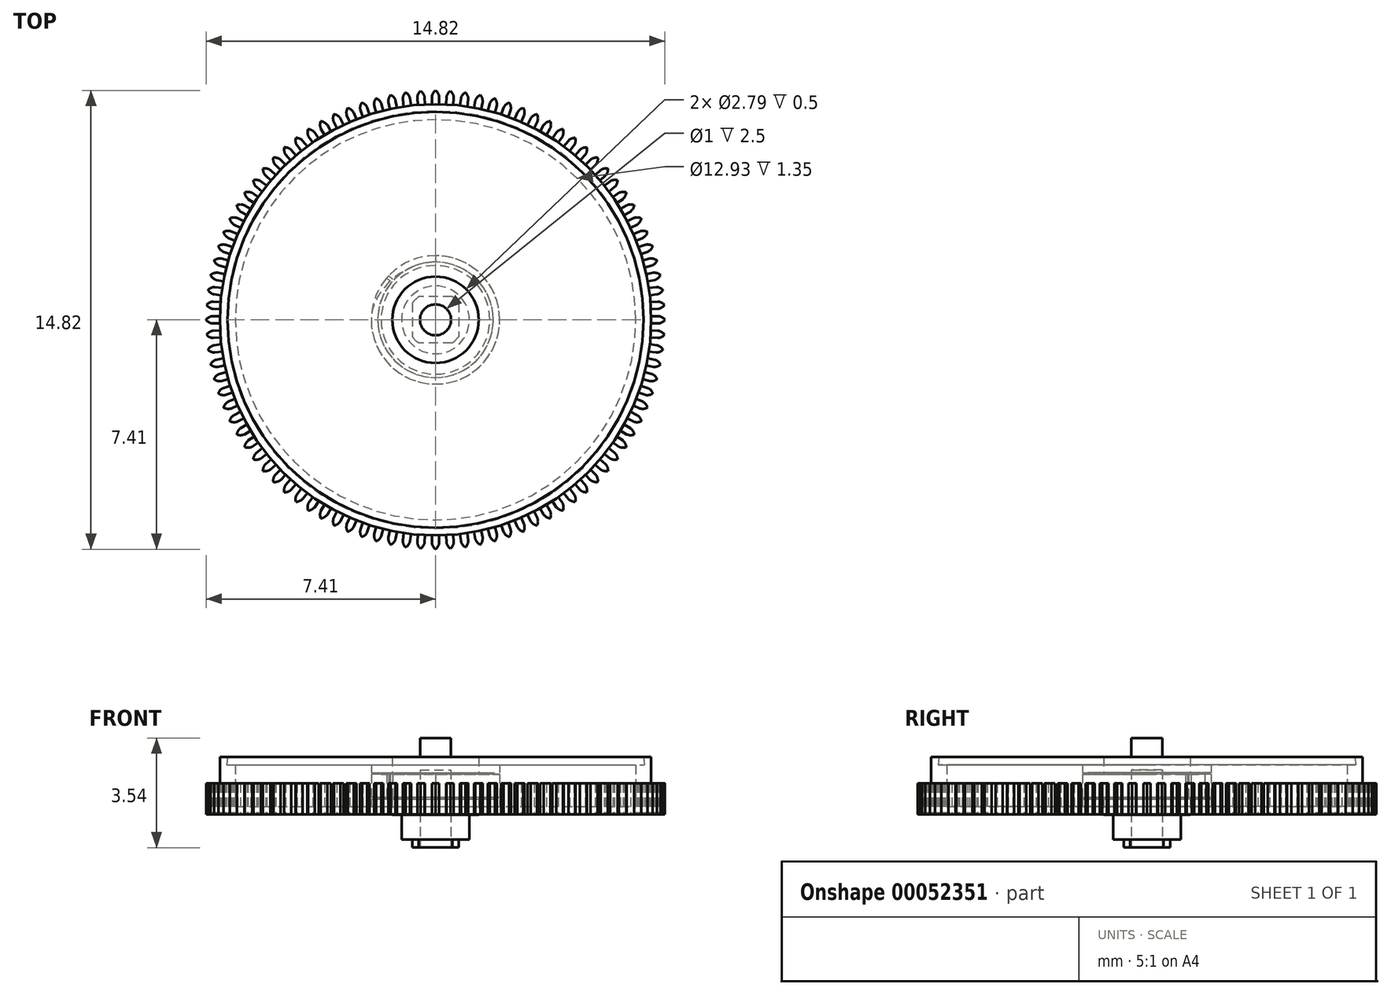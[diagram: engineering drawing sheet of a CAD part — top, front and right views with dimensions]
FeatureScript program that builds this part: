
annotation { "Feature Type Name" : "Feature", "Feature Type Description" : "" }
export const myFeature = defineFeature(function(context is Context, id is Id, definition is map)
    precondition{}
    {
        {
            var Q0;
            Q0=qCreatedBy(makeId("Front.planeOp"),FACE);
            var sketch = newSketch(context, id + "F0", { "sketchPlane" : qUnion([Q0])});
            skLineSegment(sketch, "E0", {"start": v(0, 0) * mm, "end": v(-2.08, 0) * mm, "construction": true});
            skLineSegment(sketch, "E1", {"start": v(-2.08, 0.38) * mm, "end": v(-2.08, -0.38) * mm});
            skLineSegment(sketch, "E2", {"start": v(-2.08, 0.37) * mm, "end": v(-1.75, 0.37) * mm});
            skLineSegment(sketch, "E3", {"start": v(-1.75, 0.37) * mm, "end": v(-1.75, 0.42) * mm});
            skLineSegment(sketch, "E4", {"start": v(-1.75, 0.42) * mm, "end": v(-1.4, 0.42) * mm});
            skLineSegment(sketch, "E5", {"start": v(-1.4, 0.42) * mm, "end": v(-1.4, 0.94) * mm});
            skLineSegment(sketch, "E6", {"start": v(-1.4, 0.94) * mm, "end": v(-0.5, 0.94) * mm});
            skLineSegment(sketch, "E7", {"start": v(-0.5, 0.94) * mm, "end": v(-0.5, 1.53) * mm});
            skLineSegment(sketch, "E8", {"start": v(-0.5, 1.53) * mm, "end": v(0, 1.53) * mm});
            skLineSegment(sketch, "E9", {"start": v(0, 1.53) * mm, "end": v(0, 0) * mm});
            skLineSegment(sketch, "E10", {"start": v(-2.08, -0.38) * mm, "end": v(-1.87, -0.38) * mm});
            skLineSegment(sketch, "E11", {"start": v(-1.87, -0.38) * mm, "end": v(-1.87, -0.43) * mm});
            skLineSegment(sketch, "E12", {"start": v(-1.87, -0.43) * mm, "end": v(-1.4, -0.42) * mm});
            skLineSegment(sketch, "E13", {"start": v(-1.4, -0.42) * mm, "end": v(-1.4, -0.93) * mm});
            skLineSegment(sketch, "E14", {"start": v(-1.4, -0.93) * mm, "end": v(-1.1, -0.93) * mm});
            skLineSegment(sketch, "E15", {"start": v(-1.1, -0.93) * mm, "end": v(-1.1, -1.74) * mm});
            skLineSegment(sketch, "E16", {"start": v(-1.1, -1.74) * mm, "end": v(-0.93, -1.74) * mm});
            skLineSegment(sketch, "E17", {"start": v(-0.93, -1.74) * mm, "end": v(-0.93, -2) * mm});
            skLineSegment(sketch, "E18", {"start": v(-0.93, -2) * mm, "end": v(0, -2) * mm});
            skLineSegment(sketch, "E19", {"start": v(0, -2) * mm, "end": v(0, 0) * mm});
            skSolve(sketch);
        }
        {
            var Q0;
            Q0=qSketchRegion(id+"F0",true);
            var Q1;
            Q1=sQuery(id+"F0.wireOp",EDGE,"E19");
            revolve(context, id + "F1", {"entities" : qUnion([Q0]), "axis" : qUnion([Q1]), "revolveType" : RevolveType.FULL});
        }
        {
            var Q0;
            Q0=makeQuery(id+"F1.opRevolve","SWEPT_FACE",FACE,{"disambiguationData":[OSD([sQuery(id+"F0.wireOp",EDGE,"E18")])]});
            var sketch = newSketch(context, id + "F2", { "sketchPlane" : qUnion([Q0])});
            skLineSegment(sketch, "E20.rect.bottom", {"start": v(0.75, -0.75) * mm, "end": v(-0.75, -0.75) * mm});
            skLineSegment(sketch, "E20.rect.top", {"start": v(0.75, 0.75) * mm, "end": v(-0.75, 0.75) * mm});
            skLineSegment(sketch, "E20.rect.left", {"start": v(0.75, -0.75) * mm, "end": v(0.75, 0.75) * mm});
            skLineSegment(sketch, "E20.rect.right", {"start": v(-0.75, -0.75) * mm, "end": v(-0.75, 0.75) * mm});
            skPoint(sketch, "E20.rect.middle", {"position": v(0, 0) * mm});
            skCircle(sketch, "E21.0", {"center": v(0, 0) * mm, "radius": 0.93 * mm});
            skCircle(sketch, "E22", {"center": v(0, 0) * mm, "radius": 0.5 * mm});
            skSolve(sketch);
        }
        {
            var Q0;
            {var subQ0=sQuery(id+"F2.wireOp",EDGE,"E21.0");var subQ1=sQuery(id+"F2.wireOp",EDGE,"E20.rect.bottom");var subQ2=makeQuery(id+"F2.imprint","INTERSECT",VERTEX,{"disambiguationData":[OD(0.0)],"derivedFrom":[subQ1,subQ0]});Q0=makeQuery(id+"F2.imprint","IMPRINT",FACE,{"disambiguationData":[TD([[makeQuery(id+"F2.imprint","IMPRINT",EDGE,{"disambiguationData":[TD([[subQ2,-1.0]])],"derivedFrom":subQ1}),1.0]])]});}
            var Q1;
            {var subQ0=sQuery(id+"F2.wireOp",EDGE,"E21.0");var subQ1=sQuery(id+"F2.wireOp",EDGE,"E20.rect.top");var subQ2=makeQuery(id+"F2.imprint","INTERSECT",VERTEX,{"disambiguationData":[OD(0.0)],"derivedFrom":[subQ1,subQ0]});Q1=makeQuery(id+"F2.imprint","IMPRINT",FACE,{"disambiguationData":[TD([[makeQuery(id+"F2.imprint","IMPRINT",EDGE,{"disambiguationData":[TD([[subQ2,-1.0]])],"derivedFrom":subQ1}),-1.0]])]});}
            var Q2;
            {var subQ0=sQuery(id+"F2.wireOp",EDGE,"E21.0");var subQ1=sQuery(id+"F2.wireOp",EDGE,"E20.rect.left");var subQ2=makeQuery(id+"F2.imprint","INTERSECT",VERTEX,{"disambiguationData":[OD(0.0)],"derivedFrom":[subQ1,subQ0]});Q2=makeQuery(id+"F2.imprint","IMPRINT",FACE,{"disambiguationData":[TD([[makeQuery(id+"F2.imprint","IMPRINT",EDGE,{"disambiguationData":[TD([[subQ2,-1.0]])],"derivedFrom":subQ1}),-1.0]])]});}
            var Q3;
            {var subQ0=sQuery(id+"F2.wireOp",EDGE,"E21.0");var subQ1=sQuery(id+"F2.wireOp",EDGE,"E20.rect.right");var subQ2=makeQuery(id+"F2.imprint","INTERSECT",VERTEX,{"disambiguationData":[OD(0.0)],"derivedFrom":[subQ1,subQ0]});Q3=makeQuery(id+"F2.imprint","IMPRINT",FACE,{"disambiguationData":[TD([[makeQuery(id+"F2.imprint","IMPRINT",EDGE,{"disambiguationData":[TD([[subQ2,-1.0]])],"derivedFrom":subQ1}),1.0]])]});}
            var Q4;
            Q4=makeQuery(id+"F1.opRevolve","SWEPT_FACE",FACE,{"disambiguationData":[OSD([sQuery(id+"F0.wireOp",EDGE,"E16")])]});
            extrude(context, id + "F3", {"entities" : qUnion([Q0, Q1, Q2, Q3]), "operationType" : NewBodyOperationType.REMOVE, "endBound" : BoundingType.UP_TO_SURFACE, "oppositeDirection" : true, "endBoundEntityFace" : qUnion([Q4]), "depth" : 25 * mm});
        }
        {
            var Q0;
            Q0=makeQuery(id+"F2.imprint","IMPRINT",FACE,{"disambiguationData":[TD([[makeQuery(id+"F2.imprint","IMPRINT",EDGE,{"derivedFrom":sQuery(id+"F2.wireOp",EDGE,"E22")}),1.0]])]});
            extrude(context, id + "F4", {"entities" : qUnion([Q0]), "operationType" : NewBodyOperationType.REMOVE, "oppositeDirection" : true, "depth" : 2.5 * mm});
        }
        {
            var Q0;
            Q0=makeQuery(id+"F1.opRevolve","SWEPT_FACE",FACE,{"disambiguationData":[OSD([sQuery(id+"F0.wireOp",EDGE,"E10")])]});
            var sketch = newSketch(context, id + "F5", { "sketchPlane" : qUnion([Q0])});
            skLineSegment(sketch, "E23", {"start": v(0, 0) * mm, "end": v(0, -1.86) * mm, "construction": true});
            skCircle(sketch, "E24.0", {"center": v(0, 0) * mm, "radius": 2.08 * mm});
            skCircle(sketch, "E25.0", {"center": v(0, 0) * mm, "radius": 1.87 * mm});
            skLineSegment(sketch, "E26", {"start": v(0, -1.86) * mm, "end": v(0, -2.08) * mm});
            skFitSpline(sketch, "E27", {"points": [v(0, -1.86) * mm, v(-2.08, 0) * mm], "startDerivative": vector(-3.11, 0) * mm, "endDerivative": vector(0, 2.8) * mm});
            skLineSegment(sketch, "E28", {"start": v(-2.08, 0) * mm, "end": v(-2.08, -1.86) * mm, "construction": true});
            skLineSegment(sketch, "E29", {"start": v(-2.08, -1.86) * mm, "end": v(0, -1.86) * mm, "construction": true});
            skLineSegment(sketch, "E30", {"start": v(0, 0) * mm, "end": v(-2.08, -1.86) * mm, "construction": true});
            skLineSegment(sketch, "E31.0", {"start": v(-0.07, 0) * mm, "end": v(-2.08, -1.8) * mm, "construction": true});
            skLineSegment(sketch, "E32.0", {"start": v(0, -0.07) * mm, "end": v(-2, -1.87) * mm, "construction": true});
            skArc(sketch, "E33", {"start": v(-1.5, -1.42) * mm, "mid": v(-1.54, -1.39) * mm, "end": v(-1.58, -1.35) * mm});
            skLineSegment(sketch, "E34", {"start": v(-1.58, -1.35) * mm, "end": v(-1.42, -1.2) * mm});
            skLineSegment(sketch, "E35", {"start": v(-1.5, -1.42) * mm, "end": v(-1.35, -1.28) * mm});
            skSolve(sketch);
        }
        {
            var Q0;
            {var subQ0=sQuery(id+"F5.wireOp",EDGE,"E26");Q0=makeQuery(id+"F5.imprint","IMPRINT",FACE,{"disambiguationData":[TD([[makeQuery(id+"F5.imprint","IMPRINT",EDGE,{"derivedFrom":subQ0}),-1.0]])]});}
            var Q1;
            {var subQ0=sQuery(id+"F5.wireOp",EDGE,"E34");var subQ1=sQuery(id+"F5.wireOp",EDGE,"E24.0");var subQ2=makeQuery(id+"F5.imprint","INTERSECT",VERTEX,{"derivedFrom":[subQ1,subQ0]});Q1=makeQuery(id+"F5.imprint","IMPRINT",FACE,{"disambiguationData":[TD([[makeQuery(id+"F5.imprint","IMPRINT",EDGE,{"disambiguationData":[TD([[subQ2,-1.0]])],"derivedFrom":subQ1}),1.0]])]});}
            var Q2;
            {var subQ0=sQuery(id+"F5.wireOp",EDGE,"E27");var subQ1=sQuery(id+"F5.wireOp",EDGE,"E24.0");var subQ2=makeQuery(id+"F5.imprint","INTERSECT",VERTEX,{"derivedFrom":[subQ1,subQ0]});Q2=makeQuery(id+"F5.imprint","IMPRINT",FACE,{"disambiguationData":[TD([[makeQuery(id+"F5.imprint","IMPRINT",EDGE,{"disambiguationData":[TD([[subQ2,-1.0]])],"derivedFrom":subQ1}),1.0]])]});}
            extrude(context, id + "F6", {"entities" : qUnion([Q0, Q1, Q2]), "operationType" : NewBodyOperationType.REMOVE, "endBound" : BoundingType.THROUGH_ALL, "oppositeDirection" : true, "depth" : 25 * mm});
        }
        {
            var Q0;
            Q0=qCreatedBy(makeId("Top.planeOp"),FACE);
            var sketch = newSketch(context, id + "F7", { "sketchPlane" : qUnion([Q0])});
            skLineSegment(sketch, "E36.0", {"start": v(-1.58, 1.35) * mm, "end": v(-1.42, 1.2) * mm});
            skLineSegment(sketch, "E36.1", {"start": v(-1.5, 1.42) * mm, "end": v(-1.35, 1.28) * mm});
            skArc(sketch, "E36.2", {"start": v(-1.5, 1.42) * mm, "mid": v(-1.54, 1.39) * mm, "end": v(-1.58, 1.35) * mm});
            skLineSegment(sketch, "E37", {"start": v(-1.42, 1.2) * mm, "end": v(-1.35, 1.28) * mm});
            skSolve(sketch);
        }
        {
            var Q0;
            Q0=qSketchRegion(id+"F7",true);
            extrude(context, id + "F8", {"entities" : qUnion([Q0]), "operationType" : NewBodyOperationType.ADD, "depth" : 0.25 * mm, "symmetric" : true});
        }
        {
            var Q0;
            Q0=qCreatedBy(makeId("Front.planeOp"),FACE);
            var sketch = newSketch(context, id + "F9", { "sketchPlane" : qUnion([Q0])});
            skLineSegment(sketch, "E38.0", {"start": v(-1.4, -0.42) * mm, "end": v(-1.4, -0.93) * mm});
            skLineSegment(sketch, "E38.1", {"start": v(-1.87, -0.43) * mm, "end": v(-1.4, -0.42) * mm});
            skLineSegment(sketch, "E38.2", {"start": v(-2.08, 0.38) * mm, "end": v(-2.08, -0.38) * mm});
            skLineSegment(sketch, "E38.3", {"start": v(-1.4, -0.93) * mm, "end": v(-1.1, -0.93) * mm});
            skLineSegment(sketch, "E38.4", {"start": v(1.4, -0.93) * mm, "end": v(-1.4, -0.93) * mm});
            skLineSegment(sketch, "E38.5", {"start": v(-1.75, 0.42) * mm, "end": v(-1.4, 0.42) * mm});
            skLineSegment(sketch, "E38.6", {"start": v(-1.4, 0.42) * mm, "end": v(-1.4, 0.94) * mm});
            skLineSegment(sketch, "E38.7", {"start": v(-1.4, 0.94) * mm, "end": v(-0.5, 0.94) * mm});
            skLineSegment(sketch, "E39", {"start": v(-1.4, -0.92) * mm, "end": v(-6.96, -0.93) * mm});
            skLineSegment(sketch, "E40", {"start": v(-6.96, -0.93) * mm, "end": v(-6.96, 0.92) * mm});
            skLineSegment(sketch, "E41", {"start": v(-6.96, 0.92) * mm, "end": v(-6.71, 0.92) * mm});
            skLineSegment(sketch, "E42", {"start": v(-6.71, 0.93) * mm, "end": v(-6.75, 0.68) * mm});
            skLineSegment(sketch, "E43", {"start": v(-6.75, 0.67) * mm, "end": v(-6.46, 0.68) * mm});
            skLineSegment(sketch, "E44", {"start": v(-6.46, 0.68) * mm, "end": v(-6.46, -0.68) * mm});
            skLineSegment(sketch, "E45", {"start": v(-6.46, -0.68) * mm, "end": v(-2.08, -0.67) * mm});
            skLineSegment(sketch, "E46", {"start": v(-2.08, -0.67) * mm, "end": v(-2.08, -0.43) * mm});
            skLineSegment(sketch, "E47", {"start": v(-2.08, -0.43) * mm, "end": v(-1.4, -0.42) * mm});
            skLineSegment(sketch, "E48", {"start": v(-6.71, 0.92) * mm, "end": v(-1.4, 0.92) * mm});
            skLineSegment(sketch, "E49", {"start": v(-1.4, 0.92) * mm, "end": v(-1.4, 0.42) * mm});
            skLineSegment(sketch, "E50", {"start": v(-6.46, 0.68) * mm, "end": v(-2.08, 0.68) * mm});
            skPoint(sketch, "E50.endSnap0", {"position": v(-6.6, 0.68) * mm});
            skLineSegment(sketch, "E51", {"start": v(-2.08, 0.68) * mm, "end": v(-2.08, 0.42) * mm});
            skLineSegment(sketch, "E52", {"start": v(-2.08, 0.42) * mm, "end": v(-1.4, 0.42) * mm});
            skSolve(sketch);
        }
        {
            var Q0;
            {var subQ4=sQuery(id+"F9.wireOp",EDGE,"E39");Q0=makeQuery(id+"F9.imprint","IMPRINT",FACE,{"disambiguationData":[TD([[makeQuery(id+"F9.imprint","IMPRINT",EDGE,{"derivedFrom":subQ4}),-1.0]])]});}
            var Q1;
            Q1=sQuery(id+"F0.wireOp",EDGE,"E19");
            revolve(context, id + "F10", {"entities" : qUnion([Q0]), "axis" : qUnion([Q1]), "revolveType" : RevolveType.FULL});
        }
        {
            var Q0;
            Q0=makeQuery(id+"F9.imprint","IMPRINT",FACE,{"disambiguationData":[TD([[makeQuery(id+"F9.imprint","IMPRINT",EDGE,{"derivedFrom":sQuery(id+"F9.wireOp",EDGE,"E42")}),1.0]])]});
            var Q1;
            Q1=sQuery(id+"F0.wireOp",EDGE,"E19");
            revolve(context, id + "F11", {"entities" : qUnion([Q0]), "axis" : qUnion([Q1]), "revolveType" : RevolveType.FULL});
        }
        {
            var Q0;
            Q0=makeQuery(id+"F10.opRevolve","SWEPT_FACE",FACE,{"disambiguationData":[OSD([sQuery(id+"F9.wireOp",EDGE,"E39")])]});
            var sketch = newSketch(context, id + "F12", { "sketchPlane" : qUnion([Q0])});
            skCircle(sketch, "E53.0", {"center": v(0, 0) * mm, "radius": 6.96 * mm, "construction": true});
            skCircle(sketch, "E54", {"center": v(0, 0) * mm, "radius": 7.2 * mm, "construction": true});
            skCircle(sketch, "E55", {"center": v(0, 0) * mm, "radius": 7.4 * mm, "construction": true});
            skLineSegment(sketch, "E56", {"start": v(0, 0) * mm, "end": v(0, 7.4) * mm, "construction": true});
            skPoint(sketch, "E57", {"position": v(0, 7.2) * mm});
            skLineSegment(sketch, "E58", {"start": v(-0.12, 7.2) * mm, "end": v(0.12, 7.2) * mm, "construction": true});
            skCircle(sketch, "E59", {"center": v(0, 7.4) * mm, "radius": 0.29 * mm, "construction": true});
            skCircle(sketch, "E60", {"center": v(-0.12, 7.2) * mm, "radius": 0.29 * mm, "construction": true});
            skCircle(sketch, "E61", {"center": v(0.12, 7.2) * mm, "radius": 0.29 * mm, "construction": true});
            skArc(sketch, "E62", {"start": v(-0.12, 7.2) * mm, "mid": v(-0.08, 7.32) * mm, "end": v(0, 7.4) * mm});
            skArc(sketch, "E63", {"start": v(0.12, 7.2) * mm, "mid": v(0.08, 7.32) * mm, "end": v(0, 7.4) * mm});
            skLineSegment(sketch, "E64", {"start": v(-0.12, 7.2) * mm, "end": v(-0.12, 6.96) * mm});
            skLineSegment(sketch, "E65", {"start": v(-0.12, 6.96) * mm, "end": v(0.12, 6.96) * mm});
            skLineSegment(sketch, "E66", {"start": v(0.12, 6.96) * mm, "end": v(0.12, 7.2) * mm});
            skSolve(sketch);
        }
        {
            var Q0;
            Q0=qSketchRegion(id+"F12",true);
            extrude(context, id + "F13", {"entities" : qUnion([Q0]), "oppositeDirection" : true, "depth" : 1 * mm});
        }
        {
            var Q0;
            Q0=makeQuery(id+"F13.opExtrude","SWEPT_BODY",BODY,{"disambiguationData":[OSD([sQuery(id+"F12.wireOp",EDGE,"E62"),sQuery(id+"F12.wireOp",EDGE,"E63"),sQuery(id+"F12.wireOp",EDGE,"E64"),sQuery(id+"F12.wireOp",EDGE,"E65"),sQuery(id+"F12.wireOp",EDGE,"E66")])]});
            var Q1;
            Q1=makeQuery(id+"F10.opRevolve","SWEPT_EDGE",EDGE,{"disambiguationData":[OSD([sQuery(id+"F9.wireOp",EDGE,"E39"),sQuery(id+"F9.wireOp",EDGE,"E40")])]});
            circularPattern(context, id + "F14", {"entities" : qUnion([Q0]), "axis" : qUnion([Q1]), "angle" : 3.75 * degree, "instanceCount" : round(96)});
        }
    });
